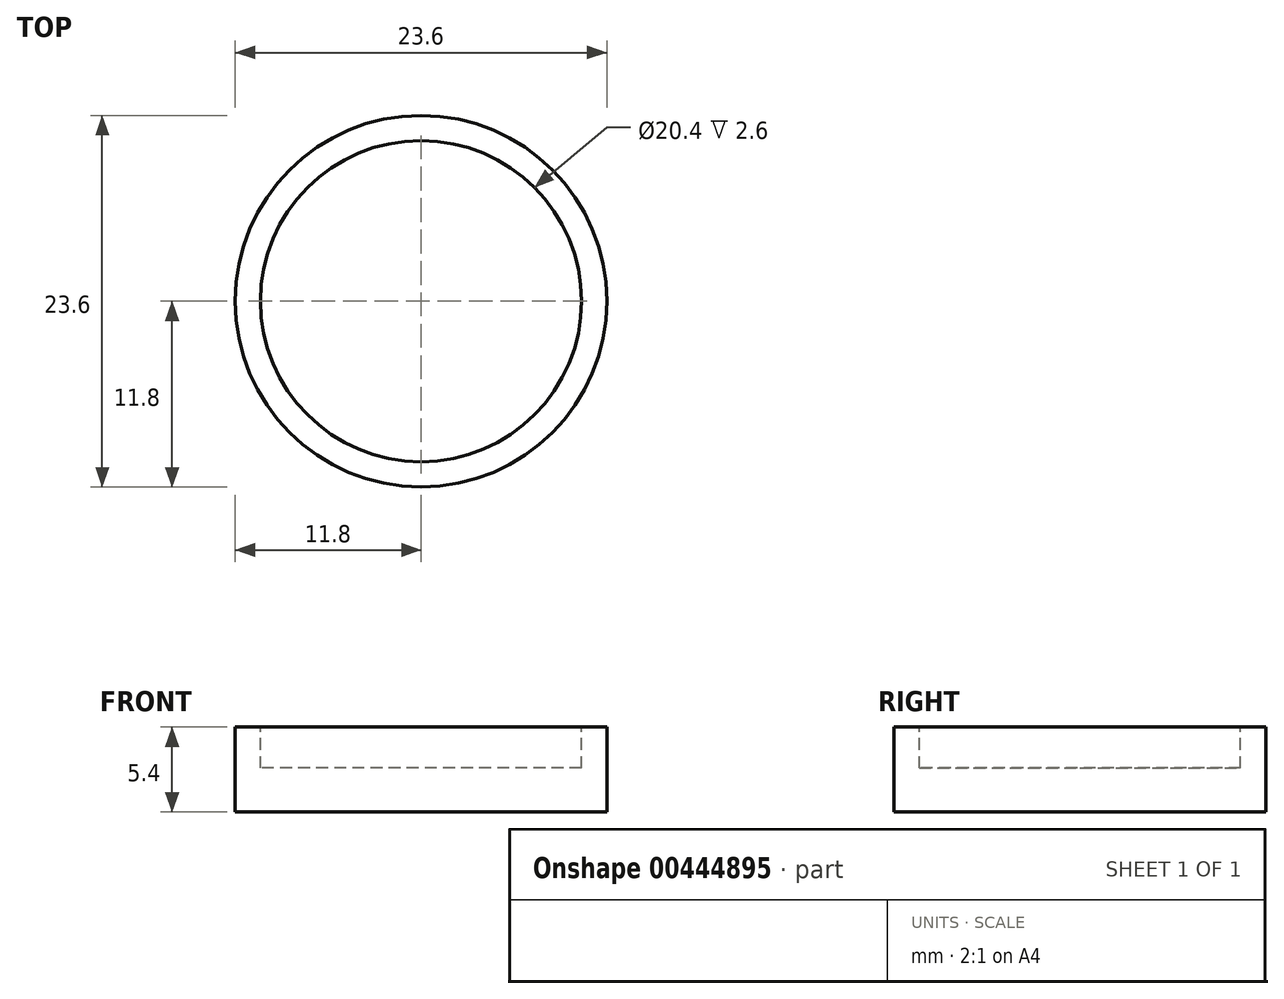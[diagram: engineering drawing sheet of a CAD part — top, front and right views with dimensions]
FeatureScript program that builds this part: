
annotation { "Feature Type Name" : "Feature", "Feature Type Description" : "" }
export const myFeature = defineFeature(function(context is Context, id is Id, definition is map)
    precondition{}
    {
        {
            var Q0;
            Q0=qCreatedBy(makeId("Top.planeOp"),FACE);
            var sketch = newSketch(context, id + "F0", { "sketchPlane" : qUnion([Q0])});
            skCircle(sketch, "E0", {"center": v(0, 0) * mm, "radius": 10 * mm});
            skSolve(sketch);
        }
        {
            var Q0;
            Q0 = qSketchRegion(id + "F0", true);
            extrude(context, id + "F1", {"entities" : qUnion([Q0]), "depth" : 1 * mm});
        }
        {
            var Q0;
            Q0=makeQuery(id+"F1.opExtrude","CAP_FACE",FACE,{"disambiguationData":[OSD([sQuery(id+"F0.wireOp",EDGE,"E0")])],"isStart":true});
            var sketch = newSketch(context, id + "F2", { "sketchPlane" : qUnion([Q0])});
            skCircle(sketch, "E1", {"center": v(0, 0) * mm, "radius": 11.8 * mm});
            skSolve(sketch);
        }
        {
            var Q0;
            Q0 = qSketchRegion(id + "F2", true);
            extrude(context, id + "F3", {"entities" : qUnion([Q0]), "depth" : 1 * mm});
        }
        {
            var Q0;
            Q0=makeQuery(id+"F3.opExtrude","CAP_FACE",FACE,{"disambiguationData":[OSD([sQuery(id+"F2.wireOp",EDGE,"E1")])],"isStart":true});
            var sketch = newSketch(context, id + "F4", { "sketchPlane" : qUnion([Q0])});
            skCircle(sketch, "E2.0", {"center": v(0, 0) * mm, "radius": 11.8 * mm});
            skCircle(sketch, "E3", {"center": v(0, 0) * mm, "radius": 10 * mm});
            skSolve(sketch);
        }
        {
            var Q0;
            Q0 = qSketchRegion(id + "F4", true);
            extrude(context, id + "F5", {"entities" : qUnion([Q0]), "operationType" : NewBodyOperationType.ADD, "depth" : 1 * mm});
        }
        {
            var Q0;
            Q0=makeQuery(id+"F5.opExtrude","CAP_FACE",FACE,{"disambiguationData":[OSD([sQuery(id+"F4.wireOp",EDGE,"E2.0"),sQuery(id+"F4.wireOp",EDGE,"E3")])],"isStart":false});
            var sketch = newSketch(context, id + "F6", { "sketchPlane" : qUnion([Q0])});
            skCircle(sketch, "E4.0.0", {"center": v(0, 0) * mm, "radius": 11.8 * mm});
            skSolve(sketch);
        }
        {
            var Q0;
            Q0 = qSketchRegion(id + "F6", true);
            extrude(context, id + "F7", {"entities" : qUnion([Q0]), "operationType" : NewBodyOperationType.ADD, "depth" : 3.4 * mm});
        }
        {
            var Q0;
            Q0=makeQuery(id+"F7.opExtrude","CAP_FACE",FACE,{"disambiguationData":[OSD([sQuery(id+"F6.wireOp",EDGE,"E4.0.0")])],"isStart":false});
            var sketch = newSketch(context, id + "F8", { "sketchPlane" : qUnion([Q0])});
            skCircle(sketch, "E5", {"center": v(0, 0) * mm, "radius": 10.2 * mm});
            skSolve(sketch);
        }
        {
            var Q0;
            Q0 = qSketchRegion(id + "F8", true);
            extrude(context, id + "F9", {"entities" : qUnion([Q0]), "operationType" : NewBodyOperationType.REMOVE, "oppositeDirection" : true, "depth" : 2.6 * mm});
        }
    });
